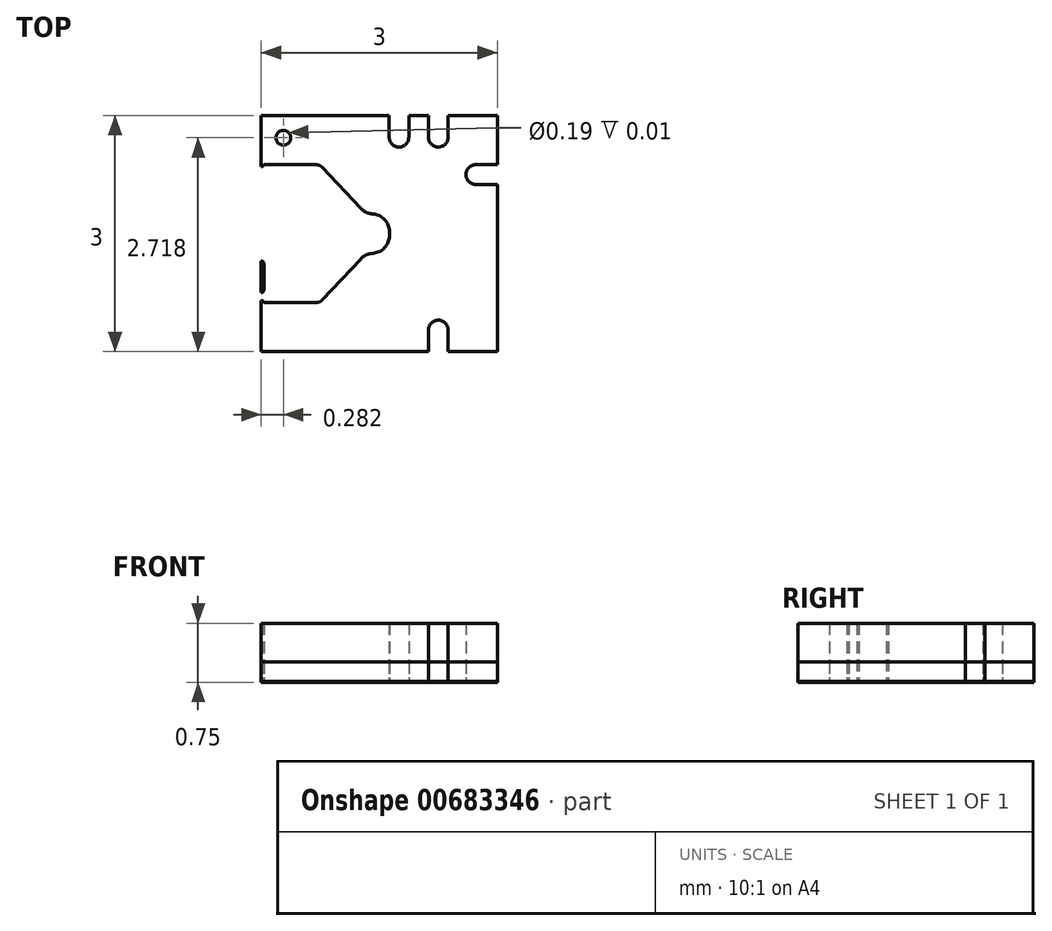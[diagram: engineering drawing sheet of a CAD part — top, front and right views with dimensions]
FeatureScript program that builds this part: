
annotation { "Feature Type Name" : "Feature", "Feature Type Description" : "" }
export const myFeature = defineFeature(function(context is Context, id is Id, definition is map)
    precondition{}
    {
        {
            var Q0;
            Q0=qCreatedBy(makeId("Top.planeOp"),FACE);
            var sketch = newSketch(context, id + "F0", { "sketchPlane" : qUnion([Q0])});
            skLineSegment(sketch, "E0.bottom", {"start": v(-1.5, 1.5) * mm, "end": v(1.5, 1.5) * mm});
            skLineSegment(sketch, "E0.top", {"start": v(-1.5, -1.5) * mm, "end": v(1.5, -1.5) * mm});
            skLineSegment(sketch, "E0.left", {"start": v(-1.5, 1.5) * mm, "end": v(-1.5, -1.5) * mm});
            skLineSegment(sketch, "E0.right", {"start": v(1.5, 1.5) * mm, "end": v(1.5, -1.5) * mm});
            skPoint(sketch, "E0.middle", {"position": v(0, 0) * mm});
            skLineSegment(sketch, "E1", {"start": v(1.5, 0) * mm, "end": v(1.5, -0.13) * mm});
            skLineSegment(sketch, "E2", {"start": v(1.5, -0.13) * mm, "end": v(1.23, -0.13) * mm});
            skLineSegment(sketch, "E3", {"start": v(1.1, -0.25) * mm, "end": v(1.1, -0.25) * mm});
            skLineSegment(sketch, "E4", {"start": v(1.23, -0.38) * mm, "end": v(1.5, -0.38) * mm});
            skLineSegment(sketch, "E5", {"start": v(1.5, -0.38) * mm, "end": v(1.5, -0.12) * mm});
            skPoint(sketch, "E6.visualSharp", {"position": v(1.1, -0.13) * mm});
            skArc(sketch, "E6.filletArc", {"start": v(1.23, -0.12) * mm, "mid": v(1.14, -0.16) * mm, "end": v(1.1, -0.25) * mm});
            skPoint(sketch, "E7.visualSharp", {"position": v(1.1, -0.38) * mm});
            skArc(sketch, "E7.filletArc", {"start": v(1.1, -0.25) * mm, "mid": v(1.14, -0.34) * mm, "end": v(1.23, -0.38) * mm});
            skLineSegment(sketch, "E8.1.0.0", {"start": v(1.5, -0.62) * mm, "end": v(1.23, -0.62) * mm});
            skLineSegment(sketch, "E8.1.0.1", {"start": v(1.23, -0.88) * mm, "end": v(1.5, -0.88) * mm});
            skLineSegment(sketch, "E8.1.0.2", {"start": v(1.5, -0.88) * mm, "end": v(1.5, -0.62) * mm});
            skArc(sketch, "E8.1.0.3", {"start": v(1.23, -0.62) * mm, "mid": v(1.14, -0.66) * mm, "end": v(1.1, -0.75) * mm});
            skArc(sketch, "E8.1.0.4", {"start": v(1.1, -0.75) * mm, "mid": v(1.14, -0.84) * mm, "end": v(1.23, -0.88) * mm});
            skPoint(sketch, "E8.1.0.5", {"position": v(1.1, -0.88) * mm});
            skPoint(sketch, "E8.1.0.6", {"position": v(1.1, -0.63) * mm});
            skLineSegment(sketch, "E8.direction1", {"start": v(1.1, -0.38) * mm, "end": v(1.1, -0.88) * mm, "construction": true});
            skLineSegment(sketch, "E9", {"start": v(0, 0) * mm, "end": v(0.34, 0) * mm});
            skPoint(sketch, "E10.MirrorP", {"position": v(1.1, 0.38) * mm});
            skPoint(sketch, "E11.MirrorP", {"position": v(1.1, 0.13) * mm});
            skPoint(sketch, "E12.MirrorP", {"position": v(1.1, 0.63) * mm});
            skArc(sketch, "E13.MirrorCS", {"start": v(1.23, 0.62) * mm, "mid": v(1.14, 0.66) * mm, "end": v(1.1, 0.75) * mm});
            skArc(sketch, "E14.MirrorCS", {"start": v(1.1, 0.75) * mm, "mid": v(1.14, 0.84) * mm, "end": v(1.23, 0.88) * mm});
            skLineSegment(sketch, "E15.MirrorCS", {"start": v(1.1, 0.38) * mm, "end": v(1.1, 0.88) * mm, "construction": true});
            skPoint(sketch, "E16.MirrorP", {"position": v(1.1, 0.88) * mm});
            skLineSegment(sketch, "E17.MirrorCS", {"start": v(1.5, 0.13) * mm, "end": v(1.23, 0.13) * mm});
            skLineSegment(sketch, "E18.MirrorCS", {"start": v(1.5, 0.88) * mm, "end": v(1.5, 0.62) * mm});
            skLineSegment(sketch, "E19.MirrorCS", {"start": v(1.23, 0.88) * mm, "end": v(1.5, 0.88) * mm});
            skArc(sketch, "E20.MirrorCS", {"start": v(1.1, 0.25) * mm, "mid": v(1.14, 0.34) * mm, "end": v(1.23, 0.38) * mm});
            skArc(sketch, "E21.MirrorCS", {"start": v(1.23, 0.12) * mm, "mid": v(1.14, 0.16) * mm, "end": v(1.1, 0.25) * mm});
            skLineSegment(sketch, "E22.MirrorCS", {"start": v(1.5, 0.63) * mm, "end": v(1.23, 0.63) * mm});
            skLineSegment(sketch, "E23.MirrorCS", {"start": v(1.1, 0.25) * mm, "end": v(1.1, 0.25) * mm});
            skLineSegment(sketch, "E24.MirrorCS", {"start": v(1.23, 0.38) * mm, "end": v(1.5, 0.38) * mm});
            skLineSegment(sketch, "E25.MirrorCS", {"start": v(1.5, 0.38) * mm, "end": v(1.5, 0.12) * mm});
            skLineSegment(sketch, "E26", {"start": v(0, -1.5) * mm, "end": v(0.13, -1.5) * mm});
            skLineSegment(sketch, "E27", {"start": v(0.13, -1.5) * mm, "end": v(0.13, -1.23) * mm});
            skLineSegment(sketch, "E28", {"start": v(0.25, -1.1) * mm, "end": v(0.25, -1.1) * mm});
            skLineSegment(sketch, "E29", {"start": v(0.37, -1.23) * mm, "end": v(0.37, -1.5) * mm});
            skPoint(sketch, "E30.visualSharp", {"position": v(0.13, -1.1) * mm});
            skArc(sketch, "E30.filletArc", {"start": v(0.25, -1.1) * mm, "mid": v(0.16, -1.14) * mm, "end": v(0.13, -1.23) * mm});
            skPoint(sketch, "E31.visualSharp", {"position": v(0.37, -1.1) * mm});
            skArc(sketch, "E31.filletArc", {"start": v(0.37, -1.23) * mm, "mid": v(0.34, -1.14) * mm, "end": v(0.25, -1.1) * mm});
            skLineSegment(sketch, "E32", {"start": v(0.13, -1.5) * mm, "end": v(0.37, -1.5) * mm});
            skLineSegment(sketch, "E33.1.0.0", {"start": v(0.63, -1.5) * mm, "end": v(0.87, -1.5) * mm});
            skLineSegment(sketch, "E33.1.0.1", {"start": v(0.87, -1.23) * mm, "end": v(0.87, -1.5) * mm});
            skArc(sketch, "E33.1.0.2", {"start": v(0.87, -1.23) * mm, "mid": v(0.84, -1.14) * mm, "end": v(0.75, -1.1) * mm});
            skPoint(sketch, "E33.1.0.3", {"position": v(0.63, -1.1) * mm});
            skPoint(sketch, "E33.1.0.4", {"position": v(0.87, -1.1) * mm});
            skLineSegment(sketch, "E33.1.0.5", {"start": v(0.63, -1.5) * mm, "end": v(0.63, -1.23) * mm});
            skArc(sketch, "E33.1.0.6", {"start": v(0.75, -1.1) * mm, "mid": v(0.66, -1.14) * mm, "end": v(0.63, -1.23) * mm});
            skLineSegment(sketch, "E33.direction1", {"start": v(0.13, -1.5) * mm, "end": v(0.63, -1.5) * mm, "construction": true});
            skArc(sketch, "E34.MirrorCS", {"start": v(0.75, 1.1) * mm, "mid": v(0.66, 1.14) * mm, "end": v(0.63, 1.23) * mm});
            skArc(sketch, "E35.MirrorCS", {"start": v(0.25, 1.1) * mm, "mid": v(0.16, 1.14) * mm, "end": v(0.13, 1.23) * mm});
            skArc(sketch, "E36.MirrorCS", {"start": v(0.37, 1.23) * mm, "mid": v(0.34, 1.14) * mm, "end": v(0.25, 1.1) * mm});
            skArc(sketch, "E37.MirrorCS", {"start": v(0.87, 1.23) * mm, "mid": v(0.84, 1.14) * mm, "end": v(0.75, 1.1) * mm});
            skLineSegment(sketch, "E38.MirrorCS", {"start": v(0.13, 1.5) * mm, "end": v(0.37, 1.5) * mm});
            skLineSegment(sketch, "E39.MirrorCS", {"start": v(0.63, 1.5) * mm, "end": v(0.87, 1.5) * mm});
            skPoint(sketch, "E40.MirrorP", {"position": v(0.63, 1.1) * mm});
            skPoint(sketch, "E41.MirrorP", {"position": v(0.37, 1.1) * mm});
            skPoint(sketch, "E42.MirrorP", {"position": v(0.13, 1.1) * mm});
            skPoint(sketch, "E43.MirrorP", {"position": v(0.87, 1.1) * mm});
            skLineSegment(sketch, "E44.MirrorCS", {"start": v(0.13, 1.5) * mm, "end": v(0.13, 1.23) * mm});
            skLineSegment(sketch, "E45.MirrorCS", {"start": v(0.25, 1.1) * mm, "end": v(0.25, 1.1) * mm});
            skLineSegment(sketch, "E46.MirrorCS", {"start": v(0.13, 1.5) * mm, "end": v(0.63, 1.5) * mm, "construction": true});
            skLineSegment(sketch, "E47.MirrorCS", {"start": v(0.63, 1.5) * mm, "end": v(0.63, 1.23) * mm});
            skLineSegment(sketch, "E48.MirrorCS", {"start": v(0.87, 1.23) * mm, "end": v(0.87, 1.5) * mm});
            skLineSegment(sketch, "E49.MirrorCS", {"start": v(0.37, 1.23) * mm, "end": v(0.37, 1.5) * mm});
            skLineSegment(sketch, "E50", {"start": v(-1.5, 0) * mm, "end": v(-1.5, -0.25) * mm});
            skLineSegment(sketch, "E51", {"start": v(-1.5, 0) * mm, "end": v(-1.5, 0.25) * mm});
            skLineSegment(sketch, "E52", {"start": v(-1.5, 0.25) * mm, "end": v(-1.5, 0.15) * mm});
            skLineSegment(sketch, "E53", {"start": v(-1.5, 0.25) * mm, "end": v(-1.5, 0.35) * mm});
            skLineSegment(sketch, "E54", {"start": v(-1.5, 0.25) * mm, "end": v(-1.5, 0.75) * mm});
            skLineSegment(sketch, "E55", {"start": v(-1.5, 0.75) * mm, "end": v(-1.5, 0.65) * mm});
            skLineSegment(sketch, "E56", {"start": v(-1.5, 0.75) * mm, "end": v(-1.5, 0.85) * mm});
            skLineSegment(sketch, "E57", {"start": v(-1.5, 0.85) * mm, "end": v(-1.48, 0.85) * mm});
            skLineSegment(sketch, "E58", {"start": v(-1.48, 0.85) * mm, "end": v(-1.46, 0.87) * mm});
            skLineSegment(sketch, "E59", {"start": v(-1.5, 0.75) * mm, "end": v(-1.48, 0.75) * mm});
            skLineSegment(sketch, "E60", {"start": v(-1.48, 0.75) * mm, "end": v(-1.46, 0.73) * mm});
            skLineSegment(sketch, "E61", {"start": v(-1.5, 0.35) * mm, "end": v(-1.48, 0.35) * mm});
            skLineSegment(sketch, "E62", {"start": v(-1.48, 0.35) * mm, "end": v(-1.46, 0.37) * mm});
            skLineSegment(sketch, "E63", {"start": v(-1.46, 0.73) * mm, "end": v(-1.46, 0.37) * mm});
            skLineSegment(sketch, "E64", {"start": v(-1.5, 0.25) * mm, "end": v(-1.48, 0.25) * mm});
            skLineSegment(sketch, "E65", {"start": v(-1.48, 0.25) * mm, "end": v(-1.46, 0.23) * mm});
            skLineSegment(sketch, "E66", {"start": v(-1.46, 0.23) * mm, "end": v(-0.58, 0.23) * mm});
            skLineSegment(sketch, "E67", {"start": v(-0.58, 0.23) * mm, "end": v(-0.47, 0.1) * mm});
            skLineSegment(sketch, "E68", {"start": v(-0.47, 0.1) * mm, "end": v(-0.17, 0.1) * mm});
            skLineSegment(sketch, "E69", {"start": v(-0.07, 0) * mm, "end": v(-0.07, 0) * mm});
            skLineSegment(sketch, "E70", {"start": v(-1.46, 0.87) * mm, "end": v(-0.8, 0.87) * mm});
            skLineSegment(sketch, "E71", {"start": v(-0.73, 0.84) * mm, "end": v(-0.24, 0.32) * mm});
            skLineSegment(sketch, "E72", {"start": v(-0.1, 0.25) * mm, "end": v(-0.1, 0.25) * mm});
            skLineSegment(sketch, "E73", {"start": v(0.13, 0.03) * mm, "end": v(0.13, 0) * mm});
            skPoint(sketch, "E74.visualSharp", {"position": v(-0.07, 0.1) * mm});
            skArc(sketch, "E74.filletArc", {"start": v(-0.07, 0) * mm, "mid": v(-0.1, 0.07) * mm, "end": v(-0.17, 0.1) * mm});
            skPoint(sketch, "E75.visualSharp", {"position": v(0.13, 0.25) * mm});
            skArc(sketch, "E75.filletArc", {"start": v(0.13, 0.03) * mm, "mid": v(0.07, 0.18) * mm, "end": v(-0.08, 0.25) * mm});
            skPoint(sketch, "E76.newPointA", {"position": v(-0.15, 0.23) * mm});
            skArc(sketch, "E76.filletArc", {"start": v(-0.24, 0.32) * mm, "mid": v(-0.17, 0.27) * mm, "end": v(-0.08, 0.25) * mm});
            skPoint(sketch, "E77.visualSharp", {"position": v(-0.76, 0.87) * mm});
            skArc(sketch, "E77.filletArc", {"start": v(-0.73, 0.84) * mm, "mid": v(-0.76, 0.87) * mm, "end": v(-0.8, 0.87) * mm});
            skLineSegment(sketch, "E78.MirrorCS", {"start": v(-1.5, -0.75) * mm, "end": v(-1.5, -0.85) * mm});
            skLineSegment(sketch, "E79.MirrorCS", {"start": v(-1.5, -0.85) * mm, "end": v(-1.48, -0.85) * mm});
            skLineSegment(sketch, "E80.MirrorCS", {"start": v(-1.48, -0.85) * mm, "end": v(-1.46, -0.87) * mm});
            skLineSegment(sketch, "E81.MirrorCS", {"start": v(-1.46, -0.87) * mm, "end": v(-0.8, -0.87) * mm});
            skArc(sketch, "E82.MirrorCS", {"start": v(-0.73, -0.84) * mm, "mid": v(-0.76, -0.87) * mm, "end": v(-0.8, -0.87) * mm});
            skLineSegment(sketch, "E83.MirrorCS", {"start": v(-0.73, -0.84) * mm, "end": v(-0.24, -0.32) * mm});
            skArc(sketch, "E84.MirrorCS", {"start": v(-0.24, -0.32) * mm, "mid": v(-0.17, -0.27) * mm, "end": v(-0.08, -0.25) * mm});
            skArc(sketch, "E85.MirrorCS", {"start": v(0.13, -0.03) * mm, "mid": v(0.07, -0.18) * mm, "end": v(-0.08, -0.25) * mm});
            skLineSegment(sketch, "E86.MirrorCS", {"start": v(0.13, -0.03) * mm, "end": v(0.13, 0) * mm});
            skArc(sketch, "E87.MirrorCS", {"start": v(-0.07, 0) * mm, "mid": v(-0.1, -0.07) * mm, "end": v(-0.17, -0.1) * mm});
            skLineSegment(sketch, "E88.MirrorCS", {"start": v(-0.47, -0.1) * mm, "end": v(-0.17, -0.1) * mm});
            skLineSegment(sketch, "E89.MirrorCS", {"start": v(-0.58, -0.23) * mm, "end": v(-0.47, -0.1) * mm});
            skLineSegment(sketch, "E90.MirrorCS", {"start": v(-1.46, -0.23) * mm, "end": v(-0.58, -0.23) * mm});
            skLineSegment(sketch, "E91.MirrorCS", {"start": v(-1.48, -0.25) * mm, "end": v(-1.46, -0.23) * mm});
            skLineSegment(sketch, "E92.MirrorCS", {"start": v(-1.5, -0.25) * mm, "end": v(-1.48, -0.25) * mm});
            skLineSegment(sketch, "E93.MirrorCS", {"start": v(-1.5, -0.35) * mm, "end": v(-1.48, -0.35) * mm});
            skLineSegment(sketch, "E94.MirrorCS", {"start": v(-1.48, -0.35) * mm, "end": v(-1.46, -0.37) * mm});
            skLineSegment(sketch, "E95.MirrorCS", {"start": v(-1.46, -0.73) * mm, "end": v(-1.46, -0.37) * mm});
            skLineSegment(sketch, "E96.MirrorCS", {"start": v(-1.48, -0.75) * mm, "end": v(-1.46, -0.73) * mm});
            skLineSegment(sketch, "E97", {"start": v(-1.5, -0.25) * mm, "end": v(-1.5, -0.35) * mm});
            skLineSegment(sketch, "E98", {"start": v(-1.48, -0.75) * mm, "end": v(-1.5, -0.75) * mm});
            skSolve(sketch);
        }
        {
            var Q0;
            Q0=makeQuery(id+"F0.imprint","IMPRINT",FACE,{"disambiguationData":[TD([[makeQuery(id+"F0.imprint","IMPRINT",EDGE,{"derivedFrom":sQuery(id+"F0.wireOp",EDGE,"E17.MirrorCS")}),-1.0]])]});
            var Q1;
            Q1=makeQuery(id+"F0.imprint","IMPRINT",FACE,{"disambiguationData":[TD([[makeQuery(id+"F0.imprint","IMPRINT",EDGE,{"derivedFrom":sQuery(id+"F0.wireOp",EDGE,"E27")}),-1.0]])]});
            var Q2;
            Q2=makeQuery(id+"F0.imprint","IMPRINT",FACE,{"disambiguationData":[TD([[makeQuery(id+"F0.imprint","IMPRINT",EDGE,{"derivedFrom":sQuery(id+"F0.wireOp",EDGE,"E33.1.0.0")}),1.0]])]});
            var Q3;
            Q3=makeQuery(id+"F0.imprint","IMPRINT",FACE,{"disambiguationData":[TD([[makeQuery(id+"F0.imprint","IMPRINT",EDGE,{"derivedFrom":sQuery(id+"F0.wireOp",EDGE,"E13.MirrorCS")}),-1.0]])]});
            var Q4;
            Q4=makeQuery(id+"F0.imprint","IMPRINT",FACE,{"disambiguationData":[TD([[makeQuery(id+"F0.imprint","IMPRINT",EDGE,{"derivedFrom":sQuery(id+"F0.wireOp",EDGE,"E8.1.0.0")}),1.0]])]});
            var Q5;
            Q5=makeQuery(id+"F0.imprint","IMPRINT",FACE,{"disambiguationData":[TD([[makeQuery(id+"F0.imprint","IMPRINT",EDGE,{"derivedFrom":sQuery(id+"F0.wireOp",EDGE,"E2")}),1.0]])]});
            var Q6;
            Q6=makeQuery(id+"F0.imprint","IMPRINT",FACE,{"disambiguationData":[TD([[makeQuery(id+"F0.imprint","IMPRINT",EDGE,{"derivedFrom":sQuery(id+"F0.wireOp",EDGE,"E34.MirrorCS")}),-1.0]])]});
            var Q7;
            Q7=makeQuery(id+"F0.imprint","IMPRINT",FACE,{"disambiguationData":[TD([[makeQuery(id+"F0.imprint","IMPRINT",EDGE,{"derivedFrom":sQuery(id+"F0.wireOp",EDGE,"E35.MirrorCS")}),-1.0]])]});
            var Q8;
            Q8=makeQuery(id+"F0.imprint","IMPRINT",FACE,{"disambiguationData":[TD([[makeQuery(id+"F0.imprint","IMPRINT",EDGE,{"derivedFrom":sQuery(id+"F0.wireOp",EDGE,"E50")}),1.0]])]});
            var Q9;
            Q9=makeQuery(id+"F0.imprint","IMPRINT",FACE,{"disambiguationData":[TD([[makeQuery(id+"F0.imprint","IMPRINT",EDGE,{"derivedFrom":sQuery(id+"F0.wireOp",EDGE,"E56")}),-1.0]])]});
            var Q10;
            {var subQ27=sQuery(id+"F0.wireOp",EDGE,"E1");Q10=makeQuery(id+"F0.imprint","IMPRINT",FACE,{"disambiguationData":[TD([[makeQuery(id+"F0.imprint","IMPRINT",EDGE,{"derivedFrom":subQ27}),-1.0]])]});}
            var Q11;
            {var subQ0=sQuery(id+"F0.wireOp",EDGE,"E55");Q11=makeQuery(id+"F0.imprint","IMPRINT",FACE,{"disambiguationData":[TD([[makeQuery(id+"F0.imprint","IMPRINT",EDGE,{"derivedFrom":subQ0}),1.0]])]});}
            var Q12;
            {var subQ0=sQuery(id+"F0.wireOp",EDGE,"E93.MirrorCS");Q12=makeQuery(id+"F0.imprint","IMPRINT",FACE,{"disambiguationData":[TD([[makeQuery(id+"F0.imprint","IMPRINT",EDGE,{"derivedFrom":subQ0}),-1.0]])]});}
            extrude(context, id + "F1", {"entities" : qUnion([Q0, Q1, Q2, Q3, Q4, Q5, Q6, Q7, Q8, Q9, Q10, Q11, Q12]), "depth" : 0.74 * mm, "offsetDistance" : 25 * mm});
        }
        {
            var Q0;
            Q0=makeQuery(id+"F0.imprint","IMPRINT",FACE,{"disambiguationData":[TD([[makeQuery(id+"F0.imprint","IMPRINT",EDGE,{"derivedFrom":sQuery(id+"F0.wireOp",EDGE,"E35.MirrorCS")}),-1.0]])]});
            var Q1;
            Q1=makeQuery(id+"F0.imprint","IMPRINT",FACE,{"disambiguationData":[TD([[makeQuery(id+"F0.imprint","IMPRINT",EDGE,{"derivedFrom":sQuery(id+"F0.wireOp",EDGE,"E34.MirrorCS")}),-1.0]])]});
            var Q2;
            Q2=makeQuery(id+"F0.imprint","IMPRINT",FACE,{"disambiguationData":[TD([[makeQuery(id+"F0.imprint","IMPRINT",EDGE,{"derivedFrom":sQuery(id+"F0.wireOp",EDGE,"E13.MirrorCS")}),-1.0]])]});
            var Q3;
            Q3=makeQuery(id+"F0.imprint","IMPRINT",FACE,{"disambiguationData":[TD([[makeQuery(id+"F0.imprint","IMPRINT",EDGE,{"derivedFrom":sQuery(id+"F0.wireOp",EDGE,"E17.MirrorCS")}),-1.0]])]});
            var Q4;
            Q4=makeQuery(id+"F0.imprint","IMPRINT",FACE,{"disambiguationData":[TD([[makeQuery(id+"F0.imprint","IMPRINT",EDGE,{"derivedFrom":sQuery(id+"F0.wireOp",EDGE,"E2")}),1.0]])]});
            var Q5;
            Q5=makeQuery(id+"F0.imprint","IMPRINT",FACE,{"disambiguationData":[TD([[makeQuery(id+"F0.imprint","IMPRINT",EDGE,{"derivedFrom":sQuery(id+"F0.wireOp",EDGE,"E8.1.0.0")}),1.0]])]});
            var Q6;
            Q6=makeQuery(id+"F0.imprint","IMPRINT",FACE,{"disambiguationData":[TD([[makeQuery(id+"F0.imprint","IMPRINT",EDGE,{"derivedFrom":sQuery(id+"F0.wireOp",EDGE,"E33.1.0.0")}),1.0]])]});
            var Q7;
            Q7=makeQuery(id+"F0.imprint","IMPRINT",FACE,{"disambiguationData":[TD([[makeQuery(id+"F0.imprint","IMPRINT",EDGE,{"derivedFrom":sQuery(id+"F0.wireOp",EDGE,"E27")}),-1.0]])]});
            var Q8;
            Q8=makeQuery(id+"F0.imprint","IMPRINT",FACE,{"disambiguationData":[TD([[makeQuery(id+"F0.imprint","IMPRINT",EDGE,{"derivedFrom":sQuery(id+"F0.wireOp",EDGE,"E56")}),-1.0]])]});
            extrude(context, id + "F2", {"entities" : qUnion([Q0, Q1, Q2, Q3, Q4, Q5, Q6, Q7, Q8]), "depth" : 0.25 * mm, "offsetDistance" : 25 * mm, "hasSecondDirection" : true, "secondDirectionOppositeDirection" : true, "secondDirectionDepth" : 0.01 * mm});
        }
        {
            var Q0;
            Q0=makeQuery(id+"F1.opExtrude","CAP_FACE",FACE,{"disambiguationData":[OSD([sQuery(id+"F0.wireOp",EDGE,"E0.bottom"),sQuery(id+"F0.wireOp",EDGE,"E0.top"),sQuery(id+"F0.wireOp",EDGE,"E0.left"),sQuery(id+"F0.wireOp",EDGE,"E0.right"),sQuery(id+"F0.wireOp",EDGE,"E1"),sQuery(id+"F0.wireOp",EDGE,"E5"),sQuery(id+"F0.wireOp",EDGE,"E8.1.0.2"),sQuery(id+"F0.wireOp",EDGE,"E18.MirrorCS"),sQuery(id+"F0.wireOp",EDGE,"E25.MirrorCS"),sQuery(id+"F0.wireOp",EDGE,"E26"),sQuery(id+"F0.wireOp",EDGE,"E32"),sQuery(id+"F0.wireOp",EDGE,"E33.1.0.0"),sQuery(id+"F0.wireOp",EDGE,"E38.MirrorCS"),sQuery(id+"F0.wireOp",EDGE,"E39.MirrorCS"),sQuery(id+"F0.wireOp",EDGE,"E50"),sQuery(id+"F0.wireOp",EDGE,"E51"),sQuery(id+"F0.wireOp",EDGE,"E52"),sQuery(id+"F0.wireOp",EDGE,"E54"),sQuery(id+"F0.wireOp",EDGE,"E55"),sQuery(id+"F0.wireOp",EDGE,"E56"),sQuery(id+"F0.wireOp",EDGE,"E97"),sQuery(id+"F0.wireOp",EDGE,"E78.MirrorCS")])],"isStart":false});
            var sketch = newSketch(context, id + "F3", { "sketchPlane" : qUnion([Q0])});
            skCircle(sketch, "E99", {"center": v(-1.22, 1.22) * mm, "radius": 0.1 * mm});
            skSolve(sketch);
        }
        {
            var Q0;
            Q0=makeQuery(id+"F3.imprint","IMPRINT",FACE,{"disambiguationData":[TD([[makeQuery(id+"F3.imprint","IMPRINT",EDGE,{"derivedFrom":sQuery(id+"F3.wireOp",EDGE,"E99")}),1.0]])]});
            extrude(context, id + "F4", {"entities" : qUnion([Q0]), "operationType" : NewBodyOperationType.REMOVE, "oppositeDirection" : true, "depth" : 0.01 * mm, "offsetDistance" : 25 * mm});
        }
    });
